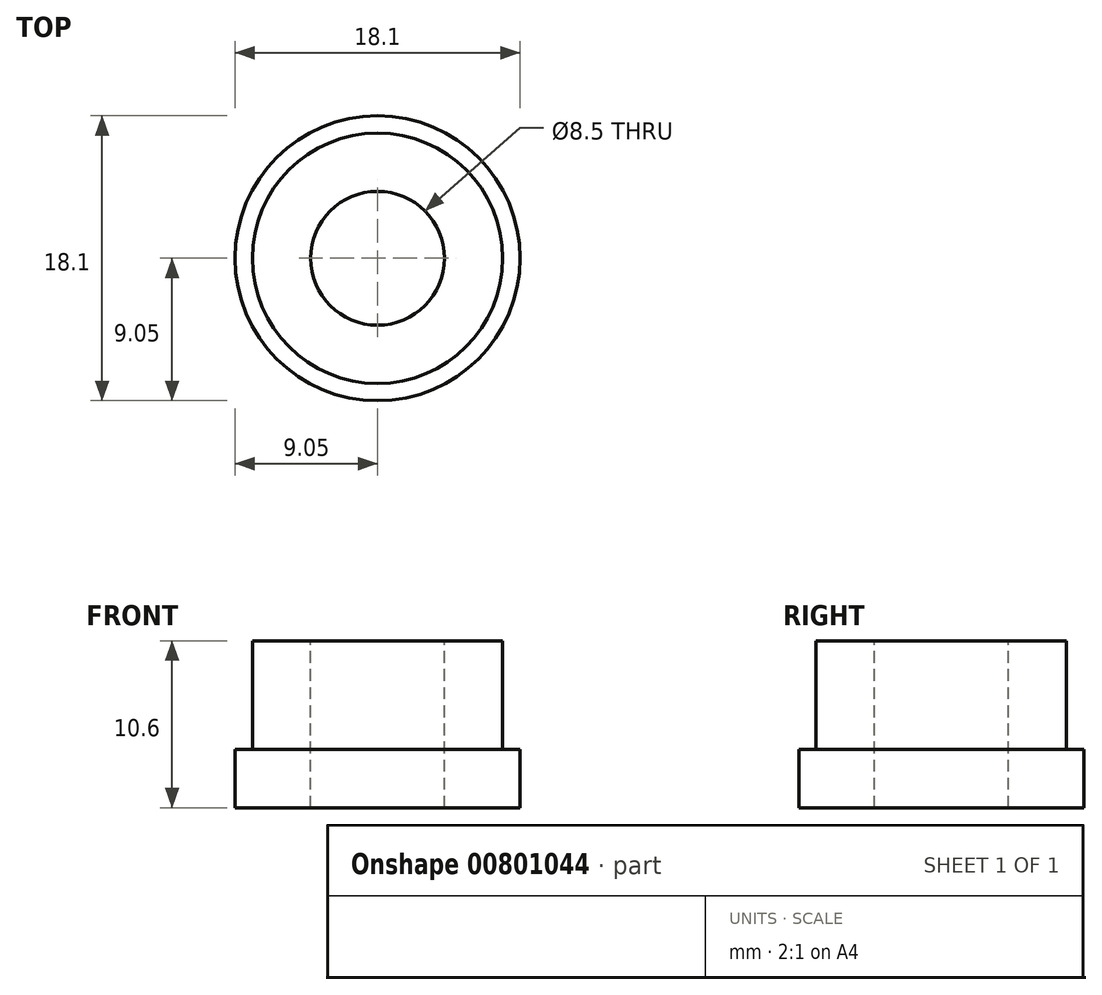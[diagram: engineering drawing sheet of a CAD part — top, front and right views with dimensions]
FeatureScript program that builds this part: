
annotation { "Feature Type Name" : "Feature", "Feature Type Description" : "" }
export const myFeature = defineFeature(function(context is Context, id is Id, definition is map)
    precondition{}
    {
        {
            var Q0;
            Q0=qCreatedBy(makeId("Front.planeOp"),FACE);
            var sketch = newSketch(context, id + "F0", { "sketchPlane" : qUnion([Q0])});
            skLineSegment(sketch, "E0", {"start": v(0, 0) * mm, "end": v(0, -10.6) * mm});
            skLineSegment(sketch, "E1", {"start": v(0, -10.6) * mm, "end": v(9.05, -10.6) * mm});
            skLineSegment(sketch, "E2", {"start": v(9.05, -10.6) * mm, "end": v(9.05, -6.9) * mm});
            skLineSegment(sketch, "E3", {"start": v(9.05, -6.9) * mm, "end": v(7.95, -6.9) * mm});
            skLineSegment(sketch, "E4", {"start": v(7.95, -6.9) * mm, "end": v(7.95, 0) * mm});
            skLineSegment(sketch, "E5", {"start": v(7.95, 0) * mm, "end": v(0, 0) * mm});
            skSolve(sketch);
        }
        {
            var Q0;
            Q0 = qSketchRegion(id + "F0", true);
            var Q1;
            Q1=sQuery(id+"F0.wireOp",EDGE,"E0");
            revolve(context, id + "F1", {"surfaceOperationType" : NewSurfaceOperationType.NEW, "entities" : qUnion([Q0]), "axis" : qUnion([Q1]), "revolveType" : RevolveType.FULL});
        }
        {
            var Q0;
            Q0=makeQuery(id+"F1.opRevolve","SWEPT_FACE",FACE,{"disambiguationData":[OSD([sQuery(id+"F0.wireOp",EDGE,"E5")])]});
            var sketch = newSketch(context, id + "F2", { "sketchPlane" : qUnion([Q0])});
            skCircle(sketch, "E6", {"center": v(0, 0) * mm, "radius": 4.25 * mm});
            skSolve(sketch);
        }
        {
            var Q0;
            Q0 = qSketchRegion(id + "F2", true);
            extrude(context, id + "F3", {"entities" : qUnion([Q0]), "operationType" : NewBodyOperationType.REMOVE, "endBound" : BoundingType.THROUGH_ALL, "oppositeDirection" : true, "depth" : 25 * mm, "offsetDistance" : 25 * mm});
        }
    });
